SOLIDWORKS PART (.sldprt)
format: sldprt  version: not decoded by parser v0  size: 414,720 bytes
history: native  units: mm
features: sketch x13, cut_revolve x6, cut_extrude x4, plane x3, revolve x2, material x1, extrude x1, chamfer x1 (+15 scaffold rows collapsed)
feature tree (46):
  scaffold x15  (default folders/planes/origin — collapsed)
  material  "AISI 316 Annealed Stainless Steel Bar (SS)"
  sketch  "Sketch1"  dims[E=28.448mm]
  extrude  "Extrude1"  [1 undecoded]
  plane  "SwitchPlaneA"  Offset=39.376mm
  plane  "SwitchPlaneB"  Offset=48.773mm
  sketch  "Sketch2"  dims[NN=15.875mm B=15.8496mm D1=2.286mm W-K=12.7mm D2=14.0mm D3=2.8mm]
  revolve  "Nose"  Angle=360deg
  sketch  "Sketch3"  dims[c1.D1=0.762mm c1.D2=0.762mm c1.D3=21.0185mm c1.D4=0.762mm c1.D5=~2.73029mm c2.D5=45.0deg c2.D2=33.697mm c2.D6=1.524mm c2.D7=0.762mm]
  cut_revolve  "CoverGrooves"  Angle=360deg
  sketch  "Sketch7"  dims[D1=10.3mm Y-K=26.67mm D2=0.7mm]
  cut_revolve  "FrontPort"  Angle=360deg
  sketch  "Sketch8"  dims[MM=7.9248mm]
  cut_extrude  "RodHole"  [1 undecoded]
  sketch  "Sketch9"  dims[Bore=26.9875mm]
  cut_extrude  "StrokeChamber"  [1 undecoded]
  chamfer  "Chamfer1"  Distance=0.5mm Angle=45deg
  sketch  "Sketch4"  dims[NC=27.448mm N=22.352mm D1=12.7mm NE=6.096mm]
  cut_extrude  "Flats"  [1 undecoded]
  sketch  "Sketch10"  dims[D1=10.3mm D2=0.7mm]
  cut_revolve  "RearStdPort"  Angle=360deg
  sketch  "Sketch11"  dims[D1=0.9676mm D2=2.286mm ZB-LB+L=15.748mm `=19.05mm D3=15.875mm D4=14.0mm]
  cut_revolve  "EndThreads"  Angle=360deg
  sketch  "Sketch13"  dims[YC=15.748mm D1=22.8581mm]
  cut_revolve  "RearTopPort"  Angle=360deg
  sketch  "Sketch12"  dims[F=9.652mm D1=15.375mm]
  cut_extrude  "EndFlats"  [1 undecoded]
  sketch  "Sketch15"  dims[G=6.3754mm L=8.636mm D1=0.5mm]
  cut_revolve  "ClevisPinHole"  Angle=360deg
  sketch  "Sketch18"  dims[c1.GB=19.05mm c1.D1=~16.465325mm c2.D1=45.0deg c3.D1=0.5mm]
  revolve  "ClevisPin"  Angle=360deg
  plane  "Plane1"
decode coverage: 22 of 27 modeling features carry decoded parameters
note: ~ marks probable driven/reference dimensions
note: 5 parameter values undecoded
summary: no parameter record found for 5 features
note: suppression state not decoded; provenance and decode notes live in map.json
